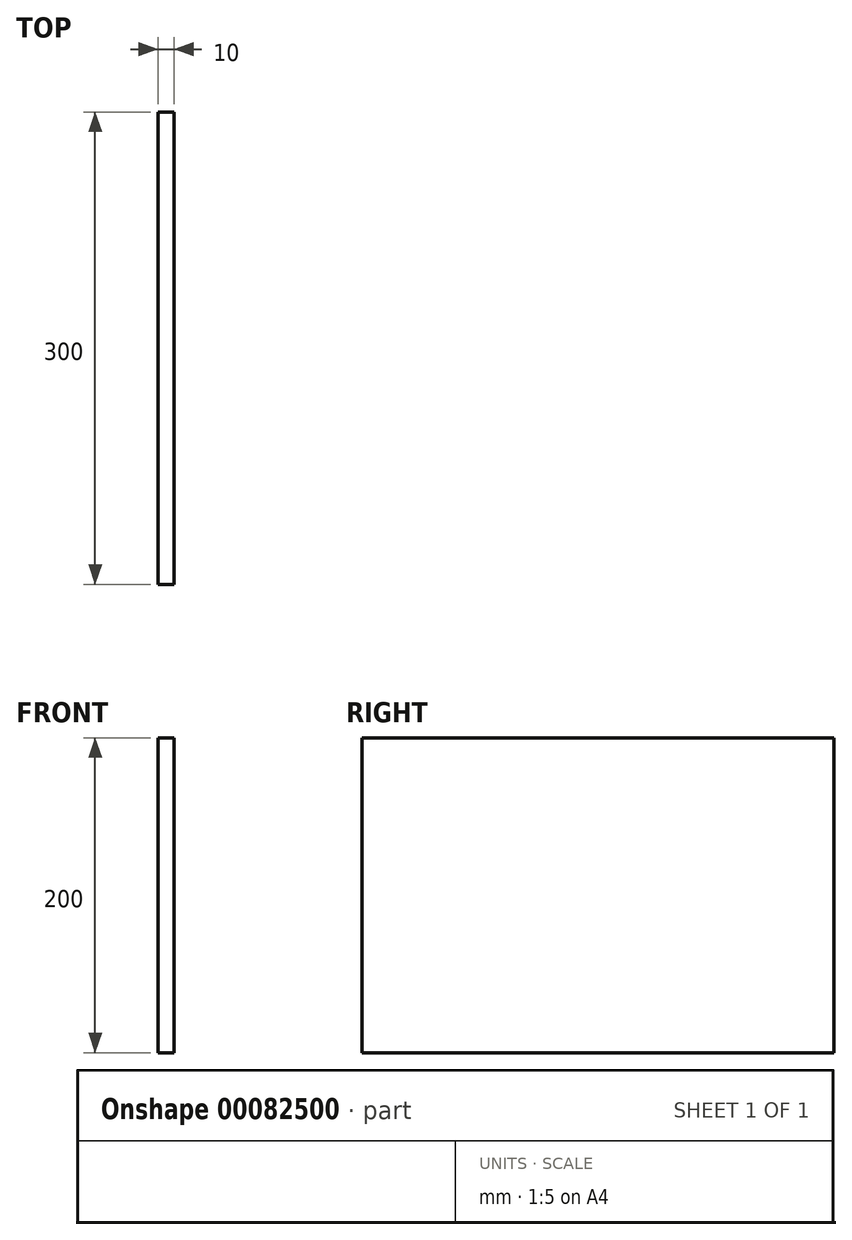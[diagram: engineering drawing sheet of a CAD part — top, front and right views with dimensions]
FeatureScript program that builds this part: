
annotation { "Feature Type Name" : "Feature", "Feature Type Description" : "" }
export const myFeature = defineFeature(function(context is Context, id is Id, definition is map)
    precondition{}
    {
        {
            var Q0;
            Q0=qCreatedBy(makeId("Right.planeOp"),FACE);
            var sketch = newSketch(context, id + "F0", { "sketchPlane" : qUnion([Q0])});
            skLineSegment(sketch, "E0.rect.bottom", {"start": v(-150, 100) * mm, "end": v(150, 100) * mm});
            skLineSegment(sketch, "E0.rect.top", {"start": v(-150, -100) * mm, "end": v(150, -100) * mm});
            skLineSegment(sketch, "E0.rect.left", {"start": v(-150, 100) * mm, "end": v(-150, -100) * mm});
            skLineSegment(sketch, "E0.rect.right", {"start": v(150, 100) * mm, "end": v(150, -100) * mm});
            skPoint(sketch, "E0.rect.middle", {"position": v(0, 0) * mm});
            skSolve(sketch);
        }
        {
            var Q0;
            Q0=qSketchRegion(id+"F0",true);
            extrude(context, id + "F1", {"entities" : qUnion([Q0]), "depth" : 10 * mm});
        }
    });
